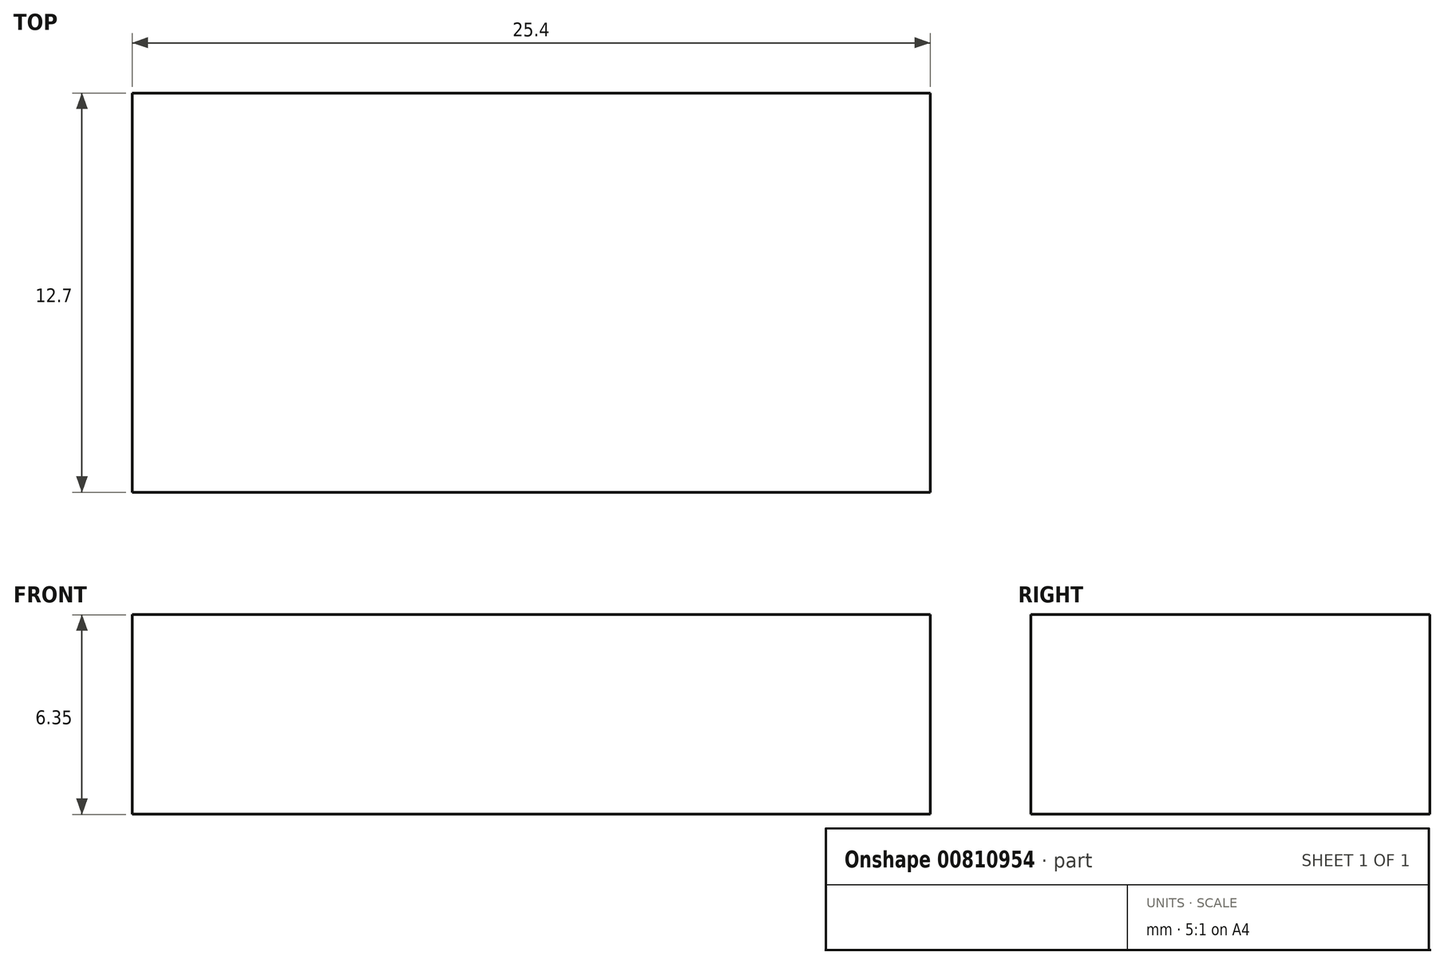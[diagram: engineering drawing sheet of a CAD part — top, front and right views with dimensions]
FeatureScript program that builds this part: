
annotation { "Feature Type Name" : "Feature", "Feature Type Description" : "" }
export const myFeature = defineFeature(function(context is Context, id is Id, definition is map)
    precondition{}
    {
        {
            var Q0;
            Q0=qCreatedBy(makeId("Right.planeOp"),FACE);
            var sketch = newSketch(context, id + "F0", { "sketchPlane" : qUnion([Q0])});
            skLineSegment(sketch, "E0.bottom", {"start": v(-4.1, 1.51) * mm, "end": v(8.6, 1.51) * mm});
            skLineSegment(sketch, "E0.top", {"start": v(-4.1, -4.84) * mm, "end": v(8.6, -4.84) * mm});
            skLineSegment(sketch, "E0.left", {"start": v(-4.1, 1.51) * mm, "end": v(-4.1, -4.84) * mm});
            skLineSegment(sketch, "E0.right", {"start": v(8.6, 1.51) * mm, "end": v(8.6, -4.84) * mm});
            skSolve(sketch);
        }
        {
            var Q0;
            Q0=makeQuery(id+"F0.imprint","IMPRINT",FACE,{"disambiguationData":[TD([[makeQuery(id+"F0.imprint","IMPRINT",EDGE,{"derivedFrom":sQuery(id+"F0.wireOp",EDGE,"E0.bottom")}),-1.0]])]});
            extrude(context, id + "F1", {"entities" : qUnion([Q0]), "depth" : 25.4 * mm, "offsetDistance" : 25.4 * mm, "symmetric" : true});
        }
    });
